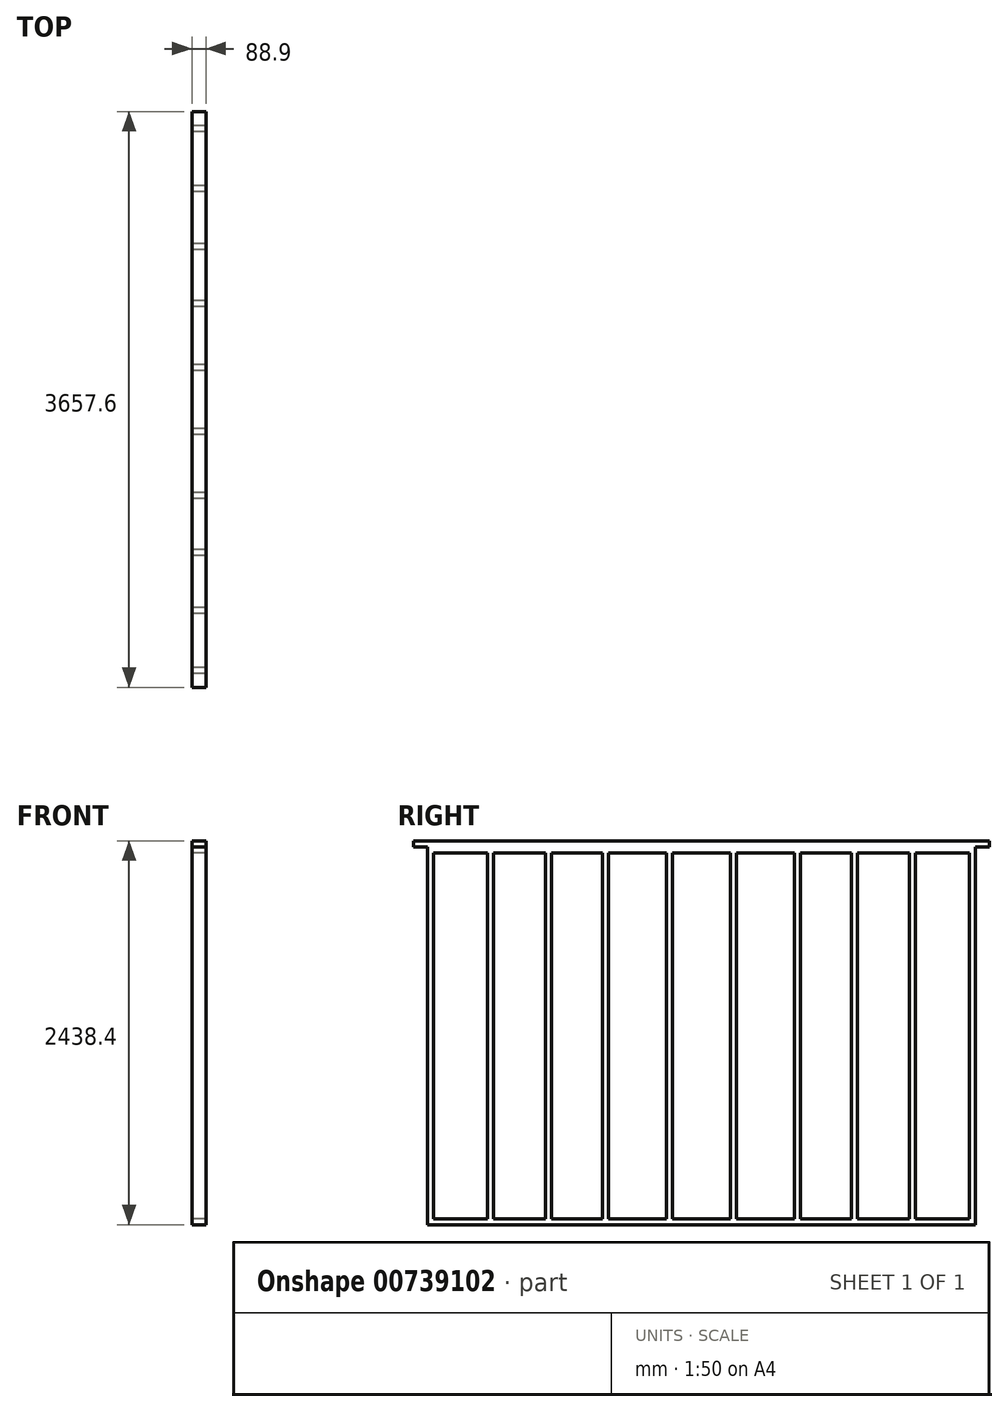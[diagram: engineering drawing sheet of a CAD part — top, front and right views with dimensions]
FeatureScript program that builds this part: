
annotation { "Feature Type Name" : "Feature", "Feature Type Description" : "" }
export const myFeature = defineFeature(function(context is Context, id is Id, definition is map)
    precondition{}
    {
        {
            var Q0;
            Q0=qCreatedBy(makeId("Right.planeOp"),FACE);
            var sketch = newSketch(context, id + "F0", { "sketchPlane" : qUnion([Q0])});
            skLineSegment(sketch, "E0.bottom", {"start": v(0, 0) * mm, "end": v(3479.8, 0) * mm});
            skLineSegment(sketch, "E0.top", {"start": v(0, 2400.3) * mm, "end": v(3479.8, 2400.3) * mm});
            skLineSegment(sketch, "E0.left", {"start": v(0, 0) * mm, "end": v(0, 2400.3) * mm});
            skLineSegment(sketch, "E0.right", {"start": v(3479.8, 0) * mm, "end": v(3479.8, 2400.3) * mm});
            skLineSegment(sketch, "E1", {"start": v(0, 38.1) * mm, "end": v(3479.8, 38.1) * mm});
            skLineSegment(sketch, "E2", {"start": v(0, 2362.2) * mm, "end": v(3479.8, 2362.2) * mm});
            skLineSegment(sketch, "E3", {"start": v(38.1, 2362.2) * mm, "end": v(38.1, 38.1) * mm});
            skLineSegment(sketch, "E4", {"start": v(3441.7, 2362.2) * mm, "end": v(3441.7, 38.1) * mm});
            skLineSegment(sketch, "E5", {"start": v(0, 2400.3) * mm, "end": v(-88.9, 2400.3) * mm});
            skLineSegment(sketch, "E6", {"start": v(-88.9, 2400.3) * mm, "end": v(-88.9, 2438.4) * mm});
            skLineSegment(sketch, "E7", {"start": v(-88.9, 2438.4) * mm, "end": v(3568.7, 2438.4) * mm});
            skLineSegment(sketch, "E8", {"start": v(3568.7, 2438.4) * mm, "end": v(3568.7, 2400.3) * mm});
            skLineSegment(sketch, "E9", {"start": v(3568.7, 2400.3) * mm, "end": v(3479.8, 2400.3) * mm});
            skLineSegment(sketch, "E10", {"start": v(1739.9, 3047.23) * mm, "end": v(1739.9, -299.9) * mm, "construction": true});
            skLineSegment(sketch, "E11", {"start": v(381, 2362.2) * mm, "end": v(381, 38.1) * mm});
            skLineSegment(sketch, "E12", {"start": v(419.1, 2362.2) * mm, "end": v(419.1, 38.1) * mm});
            skLineSegment(sketch, "E13", {"start": v(749.3, 2362.2) * mm, "end": v(749.3, 38.1) * mm});
            skLineSegment(sketch, "E14", {"start": v(787.4, 2362.2) * mm, "end": v(787.4, 38.1) * mm});
            skLineSegment(sketch, "E15", {"start": v(1111.25, 2362.2) * mm, "end": v(1111.25, 38.1) * mm});
            skLineSegment(sketch, "E16", {"start": v(1149.35, 2362.2) * mm, "end": v(1149.35, 38.1) * mm});
            skLineSegment(sketch, "E17.MirrorCS", {"start": v(2730.5, 2362.2) * mm, "end": v(2730.5, 38.1) * mm});
            skLineSegment(sketch, "E18.MirrorCS", {"start": v(2368.55, 2362.2) * mm, "end": v(2368.55, 38.1) * mm});
            skLineSegment(sketch, "E19.MirrorCS", {"start": v(3060.7, 2362.2) * mm, "end": v(3060.7, 38.1) * mm});
            skLineSegment(sketch, "E20.MirrorCS", {"start": v(3098.8, 2362.2) * mm, "end": v(3098.8, 38.1) * mm});
            skLineSegment(sketch, "E21.MirrorCS", {"start": v(2692.4, 2362.2) * mm, "end": v(2692.4, 38.1) * mm});
            skLineSegment(sketch, "E22.MirrorCS", {"start": v(2330.45, 2362.2) * mm, "end": v(2330.45, 38.1) * mm});
            skLineSegment(sketch, "E23", {"start": v(1130.3, 2843.27) * mm, "end": v(1130.3, -314.87) * mm, "construction": true});
            skLineSegment(sketch, "E24", {"start": v(2349.5, 2870.6) * mm, "end": v(2349.5, -260.23) * mm, "construction": true});
            skLineSegment(sketch, "E25", {"start": v(1517.65, 2362.2) * mm, "end": v(1517.65, 38.1) * mm});
            skLineSegment(sketch, "E26", {"start": v(1555.75, 2362.2) * mm, "end": v(1555.75, 38.1) * mm});
            skLineSegment(sketch, "E27.MirrorCS", {"start": v(1924.05, 2362.2) * mm, "end": v(1924.05, 38.1) * mm});
            skLineSegment(sketch, "E28.MirrorCS", {"start": v(1962.15, 2362.2) * mm, "end": v(1962.15, 38.1) * mm});
            skSolve(sketch);
        }
        {
            var Q0;
            {var subQ5=sQuery(id+"F0.wireOp",EDGE,"E3");Q0=makeQuery(id+"F0.imprint","IMPRINT",FACE,{"disambiguationData":[TD([[makeQuery(id+"F0.imprint","IMPRINT",EDGE,{"derivedFrom":subQ5}),-1.0]])]});}
            var Q1;
            {var subQ0=sQuery(id+"F0.wireOp",EDGE,"E11");Q1=makeQuery(id+"F0.imprint","IMPRINT",FACE,{"disambiguationData":[TD([[makeQuery(id+"F0.imprint","IMPRINT",EDGE,{"derivedFrom":subQ0}),1.0]])]});}
            var Q2;
            {var subQ0=sQuery(id+"F0.wireOp",EDGE,"E13");Q2=makeQuery(id+"F0.imprint","IMPRINT",FACE,{"disambiguationData":[TD([[makeQuery(id+"F0.imprint","IMPRINT",EDGE,{"derivedFrom":subQ0}),1.0]])]});}
            var Q3;
            {var subQ0=sQuery(id+"F0.wireOp",EDGE,"E15");Q3=makeQuery(id+"F0.imprint","IMPRINT",FACE,{"disambiguationData":[TD([[makeQuery(id+"F0.imprint","IMPRINT",EDGE,{"derivedFrom":subQ0}),1.0]])]});}
            var Q4;
            {var subQ0=sQuery(id+"F0.wireOp",EDGE,"E18.MirrorCS");Q4=makeQuery(id+"F0.imprint","IMPRINT",FACE,{"disambiguationData":[TD([[makeQuery(id+"F0.imprint","IMPRINT",EDGE,{"derivedFrom":subQ0}),-1.0]])]});}
            var Q5;
            {var subQ0=sQuery(id+"F0.wireOp",EDGE,"E17.MirrorCS");Q5=makeQuery(id+"F0.imprint","IMPRINT",FACE,{"disambiguationData":[TD([[makeQuery(id+"F0.imprint","IMPRINT",EDGE,{"derivedFrom":subQ0}),-1.0]])]});}
            var Q6;
            {var subQ0=sQuery(id+"F0.wireOp",EDGE,"E19.MirrorCS");Q6=makeQuery(id+"F0.imprint","IMPRINT",FACE,{"disambiguationData":[TD([[makeQuery(id+"F0.imprint","IMPRINT",EDGE,{"derivedFrom":subQ0}),1.0]])]});}
            var Q7;
            {var subQ5=sQuery(id+"F0.wireOp",EDGE,"E4");Q7=makeQuery(id+"F0.imprint","IMPRINT",FACE,{"disambiguationData":[TD([[makeQuery(id+"F0.imprint","IMPRINT",EDGE,{"derivedFrom":subQ5}),1.0]])]});}
            var Q8;
            {var subQ5=sQuery(id+"F0.wireOp",EDGE,"E0.top");Q8=makeQuery(id+"F0.imprint","IMPRINT",FACE,{"disambiguationData":[TD([[makeQuery(id+"F0.imprint","IMPRINT",EDGE,{"derivedFrom":subQ5}),-1.0]])]});}
            var Q9;
            Q9=makeQuery(id+"F0.imprint","IMPRINT",FACE,{"disambiguationData":[TD([[makeQuery(id+"F0.imprint","IMPRINT",EDGE,{"derivedFrom":sQuery(id+"F0.wireOp",EDGE,"E0.top")}),1.0]])]});
            var Q10;
            {var subQ8=sQuery(id+"F0.wireOp",EDGE,"E0.bottom");Q10=makeQuery(id+"F0.imprint","IMPRINT",FACE,{"disambiguationData":[TD([[makeQuery(id+"F0.imprint","IMPRINT",EDGE,{"derivedFrom":subQ8}),1.0]])]});}
            var Q11;
            {var subQ0=sQuery(id+"F0.wireOp",EDGE,"E25");Q11=makeQuery(id+"F0.imprint","IMPRINT",FACE,{"disambiguationData":[TD([[makeQuery(id+"F0.imprint","IMPRINT",EDGE,{"derivedFrom":subQ0}),1.0]])]});}
            var Q12;
            {var subQ0=sQuery(id+"F0.wireOp",EDGE,"E27.MirrorCS");Q12=makeQuery(id+"F0.imprint","IMPRINT",FACE,{"disambiguationData":[TD([[makeQuery(id+"F0.imprint","IMPRINT",EDGE,{"derivedFrom":subQ0}),1.0]])]});}
            extrude(context, id + "F1", {"entities" : qUnion([Q0, Q1, Q2, Q3, Q4, Q5, Q6, Q7, Q8, Q9, Q10, Q11, Q12]), "depth" : 88.9 * mm, "offsetDistance" : 25.4 * mm});
        }
    });
